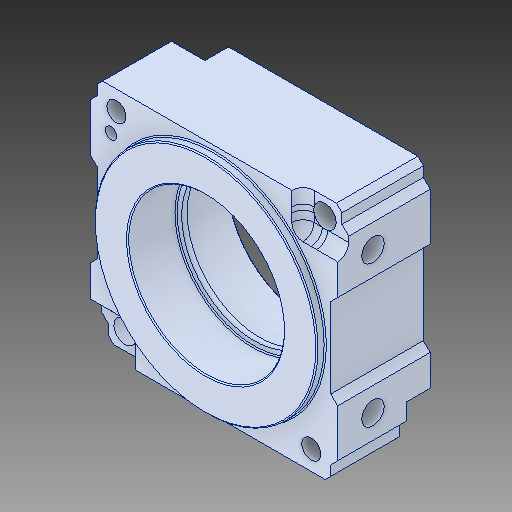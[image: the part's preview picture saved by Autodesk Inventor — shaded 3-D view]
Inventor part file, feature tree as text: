
AUTODESK INVENTOR PART (.ipt)
format: ipt  version: 2018 (Build 220112000, 112)  size: 258,560 bytes
history: native  units: in
note: dims shown in document units (in); Inventor stores cm internally (conversion verified against a paired STEP export)
features: chamfer x1
ambient origin geometry x8: Origin, YZ Plane, XZ Plane, XY Plane, X Axis, Y Axis, Z Axis, Center Point
bodies: Solid1 (feature_tree)
feature tree (1):
  chamfer  "Chamfer2"  [1 undecoded]
note: 1 required parameter value undecoded (feature->parameter linkage not recoverable at this tier; creation-order binding heuristic only, values carry confidence <= 0.55)
